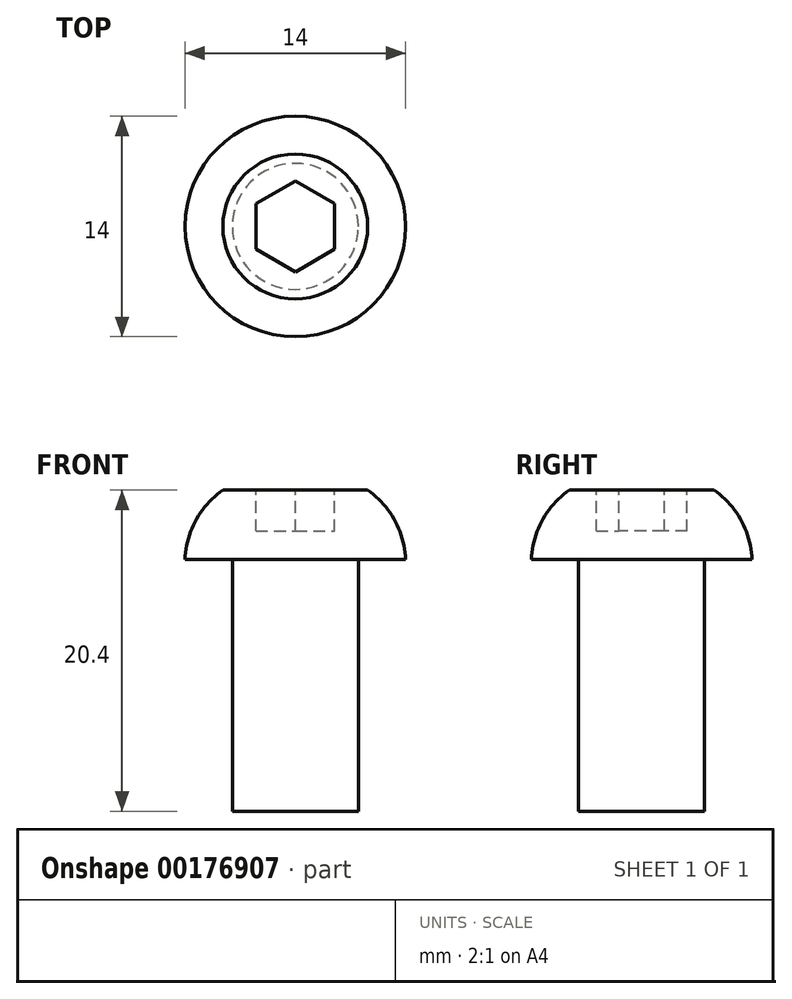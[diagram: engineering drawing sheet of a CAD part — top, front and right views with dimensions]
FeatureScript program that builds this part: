
annotation { "Feature Type Name" : "Feature", "Feature Type Description" : "" }
export const myFeature = defineFeature(function(context is Context, id is Id, definition is map)
    precondition{}
    {
        {
            var Q0;
            Q0=qCreatedBy(makeId("Top.planeOp"),FACE);
            var sketch = newSketch(context, id + "F0", { "sketchPlane" : qUnion([Q0])});
            skCircle(sketch, "E0", {"center": v(0, 0) * mm, "radius": 7 * mm});
            skSolve(sketch);
        }
        {
            var Q0;
            Q0=makeQuery(id+"F0.imprint","IMPRINT",FACE,{"disambiguationData":[TD([[makeQuery(id+"F0.imprint","IMPRINT",EDGE,{"derivedFrom":sQuery(id+"F0.wireOp",EDGE,"E0")}),1.0]])]});
            extrude(context, id + "F1", {"entities" : qUnion([Q0]), "depth" : 4.4 * mm});
        }
        {
            var Q0;
            Q0=makeQuery(id+"F1.opExtrude","CAP_FACE",FACE,{"disambiguationData":[OSD([sQuery(id+"F0.wireOp",EDGE,"E0")])],"isStart":false});
            var sketch = newSketch(context, id + "F2", { "sketchPlane" : qUnion([Q0])});
            skCircle(sketch, "E1.cCircle", {"center": v(0, 0) * mm, "radius": 2.5 * mm, "construction": true});
            skLineSegment(sketch, "E1.0", {"start": v(2.5, 1.44) * mm, "end": v(2.5, -1.44) * mm});
            skLineSegment(sketch, "E1.1", {"start": v(2.5, -1.44) * mm, "end": v(0, -2.89) * mm});
            skLineSegment(sketch, "E1.2", {"start": v(0, -2.89) * mm, "end": v(-2.5, -1.44) * mm});
            skLineSegment(sketch, "E1.3", {"start": v(-2.5, -1.44) * mm, "end": v(-2.5, 1.44) * mm});
            skLineSegment(sketch, "E1.4", {"start": v(-2.5, 1.44) * mm, "end": v(0, 2.89) * mm});
            skLineSegment(sketch, "E1.5", {"start": v(0, 2.89) * mm, "end": v(2.5, 1.44) * mm});
            skPoint(sketch, "E1.0.midPoint", {"position": v(2.5, 0) * mm});
            skSolve(sketch);
        }
        {
            var Q0;
            Q0=makeQuery(id+"F2.imprint","IMPRINT",FACE,{"disambiguationData":[TD([[makeQuery(id+"F2.imprint","IMPRINT",EDGE,{"derivedFrom":sQuery(id+"F2.wireOp",EDGE,"E1.0")}),-1.0]])]});
            extrude(context, id + "F3", {"entities" : qUnion([Q0]), "operationType" : NewBodyOperationType.REMOVE, "oppositeDirection" : true, "depth" : 2.6 * mm});
        }
        {
            var Q0;
            Q0=qCreatedBy(makeId("Right.planeOp"),FACE);
            var sketch = newSketch(context, id + "F4", { "sketchPlane" : qUnion([Q0])});
            skLineSegment(sketch, "E2.0", {"start": v(-7, 0) * mm, "end": v(7, 0) * mm});
            skLineSegment(sketch, "E3", {"start": v(-7, 0) * mm, "end": v(-7, 4.4) * mm});
            skLineSegment(sketch, "E4.0", {"start": v(-7, 4.4) * mm, "end": v(7, 4.4) * mm});
            skArc(sketch, "E5", {"start": v(-4.6, 4.4) * mm, "mid": v(-6.32, 2.48) * mm, "end": v(-7, 0) * mm});
            skLineSegment(sketch, "E6", {"start": v(0, 0) * mm, "end": v(0, 4.4) * mm, "construction": true});
            skSolve(sketch);
        }
        {
            var Q0;
            Q0=qSketchRegion(id+"F4",true);
            var Q1;
            Q1=sQuery(id+"F4.wireOp",EDGE,"E6");
            revolve(context, id + "F5", {"operationType" : NewBodyOperationType.REMOVE, "entities" : qUnion([Q0]), "axis" : qUnion([Q1]), "revolveType" : RevolveType.FULL, "oppositeDirection" : true});
        }
        {
            var Q0;
            Q0=qCreatedBy(makeId("Top.planeOp"),FACE);
            var sketch = newSketch(context, id + "F6", { "sketchPlane" : qUnion([Q0])});
            skCircle(sketch, "E7", {"center": v(0, 0) * mm, "radius": 4 * mm});
            skSolve(sketch);
        }
        {
            var Q0;
            Q0=makeQuery(id+"F6.imprint","IMPRINT",FACE,{"disambiguationData":[TD([[makeQuery(id+"F6.imprint","IMPRINT",EDGE,{"derivedFrom":sQuery(id+"F6.wireOp",EDGE,"E7")}),1.0]])]});
            extrude(context, id + "F7", {"entities" : qUnion([Q0]), "operationType" : NewBodyOperationType.ADD, "oppositeDirection" : true, "depth" : 16 * mm});
        }
    });
